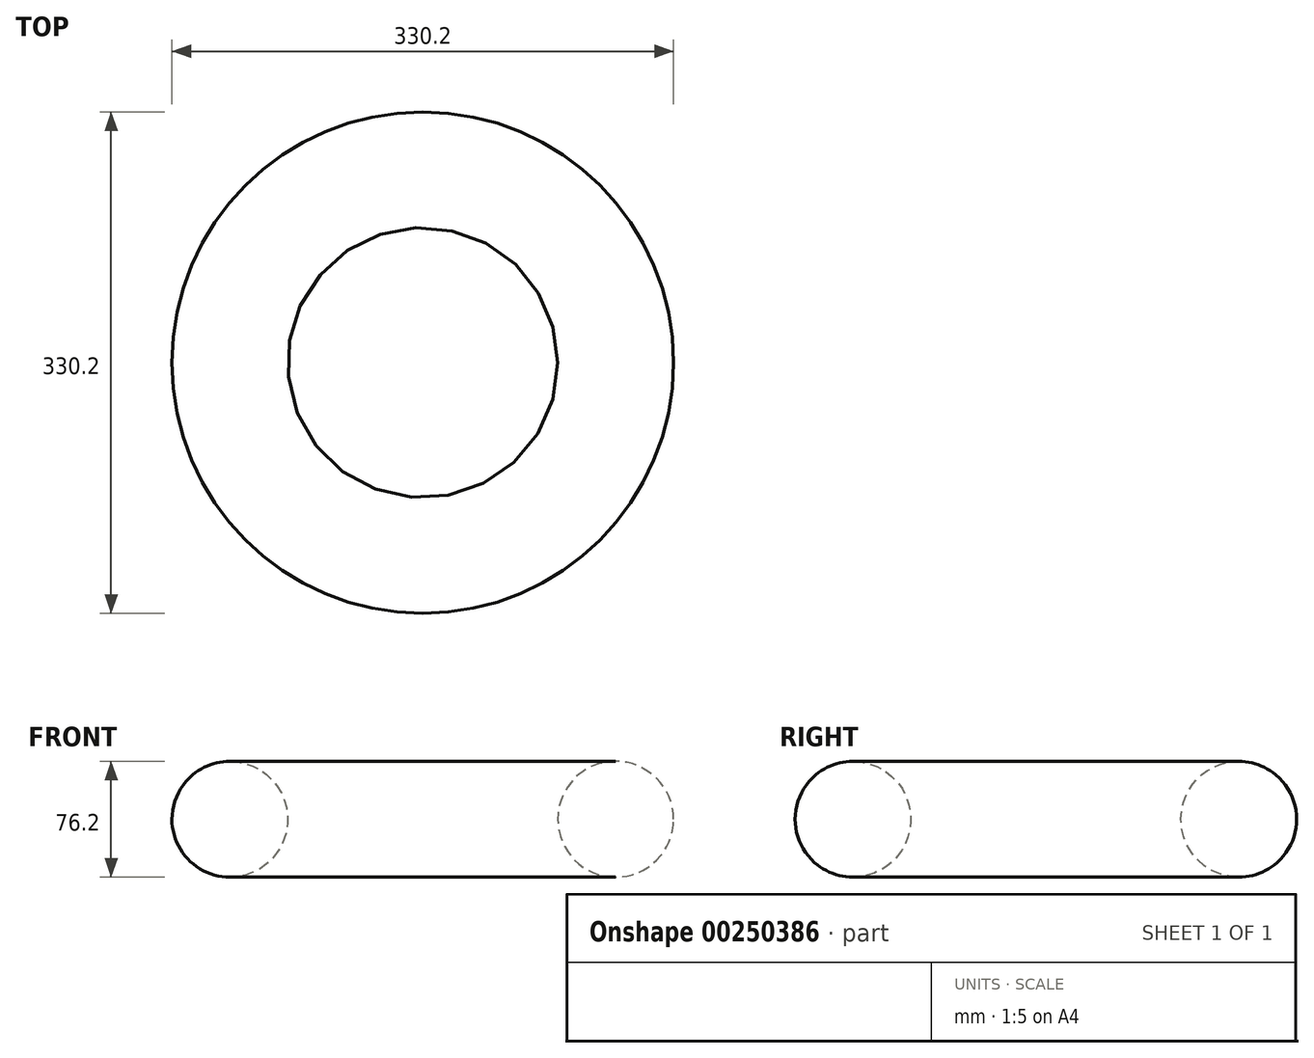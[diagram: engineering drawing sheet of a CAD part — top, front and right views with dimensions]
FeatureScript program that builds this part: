
annotation { "Feature Type Name" : "Feature", "Feature Type Description" : "" }
export const myFeature = defineFeature(function(context is Context, id is Id, definition is map)
    precondition{}
    {
        {
            var Q0;
            Q0=qCreatedBy(makeId("Front.planeOp"),FACE);
            var sketch = newSketch(context, id + "F0", { "sketchPlane" : qUnion([Q0])});
            skCircle(sketch, "E0", {"center": v(-127, 3.41) * mm, "radius": 38.1 * mm});
            skLineSegment(sketch, "E1", {"start": v(0, 0) * mm, "end": v(0, 86.02) * mm, "construction": true});
            skSolve(sketch);
        }
        {
            var Q0;
            Q0=makeQuery(id+"F0.imprint","IMPRINT",FACE,{"disambiguationData":[TD([[makeQuery(id+"F0.imprint","IMPRINT",EDGE,{"derivedFrom":sQuery(id+"F0.wireOp",EDGE,"E0")}),1.0]])]});
            var Q1;
            Q1=sQuery(id+"F0.wireOp",EDGE,"E1");
            revolve(context, id + "F1", {"entities" : qUnion([Q0]), "axis" : qUnion([Q1]), "revolveType" : RevolveType.FULL, "oppositeDirection" : true});
        }
    });
